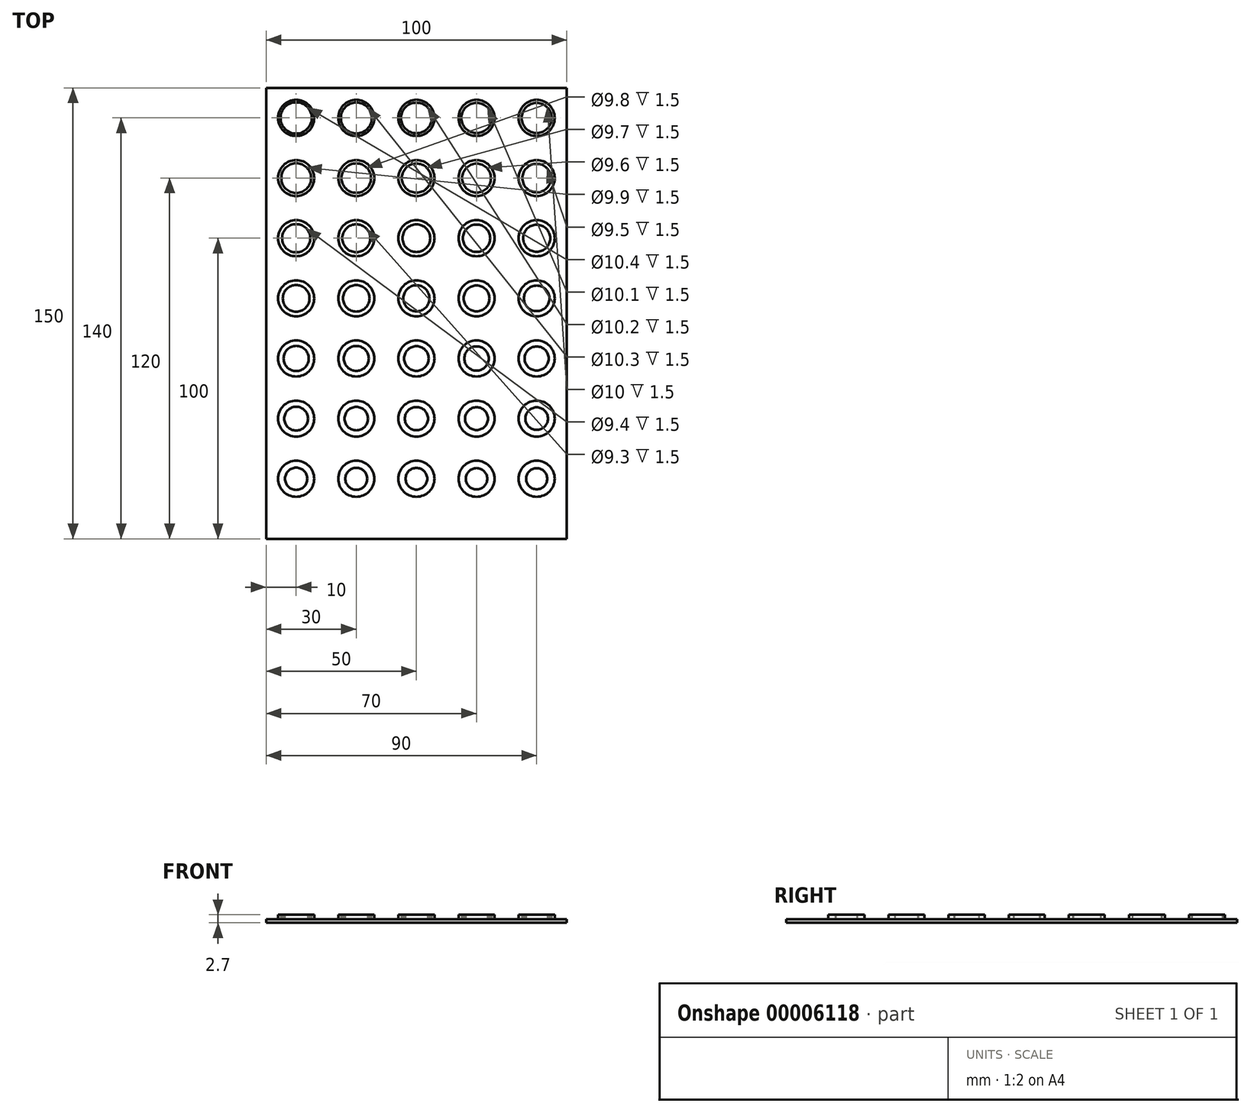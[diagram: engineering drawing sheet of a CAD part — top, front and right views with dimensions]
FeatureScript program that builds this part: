
annotation { "Feature Type Name" : "Feature", "Feature Type Description" : "" }
export const myFeature = defineFeature(function(context is Context, id is Id, definition is map)
    precondition{}
    {
        {
            var Q0;
            Q0=qCreatedBy(makeId("Top.planeOp"),FACE);
            var sketch = newSketch(context, id + "F0", { "sketchPlane" : qUnion([Q0])});
            skLineSegment(sketch, "E0.bottom", {"start": v(-10, 10) * mm, "end": v(90, 10) * mm});
            skLineSegment(sketch, "E0.top", {"start": v(-10, -140) * mm, "end": v(90, -140) * mm});
            skLineSegment(sketch, "E0.left", {"start": v(-10, 10) * mm, "end": v(-10, -140) * mm});
            skLineSegment(sketch, "E0.right", {"start": v(90, 10) * mm, "end": v(90, -140) * mm});
            skSolve(sketch);
        }
        {
            var Q0;
            Q0 = qSketchRegion(id + "F0", true);
            extrude(context, id + "F1", {"entities" : qUnion([Q0]), "depth" : 1.2 * mm});
        }
        {
            var Q0;
            Q0=makeQuery(id+"F1.opExtrude","CAP_FACE",FACE,{"disambiguationData":[OSD([sQuery(id+"F0.wireOp",EDGE,"E0.bottom"),sQuery(id+"F0.wireOp",EDGE,"E0.top"),sQuery(id+"F0.wireOp",EDGE,"E0.left"),sQuery(id+"F0.wireOp",EDGE,"E0.right")])],"isStart":false});
            var sketch = newSketch(context, id + "F2", { "sketchPlane" : qUnion([Q0])});
            skCircle(sketch, "E1", {"center": v(20, -20) * mm, "radius": 6 * mm});
            skCircle(sketch, "E2", {"center": v(20, -20) * mm, "radius": 4.9 * mm});
            skCircle(sketch, "E3", {"center": v(40, -20) * mm, "radius": 6 * mm});
            skCircle(sketch, "E4", {"center": v(40, -20) * mm, "radius": 4.85 * mm});
            skCircle(sketch, "E5", {"center": v(60, -20) * mm, "radius": 6 * mm});
            skCircle(sketch, "E6", {"center": v(60, -20) * mm, "radius": 4.8 * mm});
            skCircle(sketch, "E7", {"center": v(0, -20) * mm, "radius": 6 * mm});
            skCircle(sketch, "E8", {"center": v(0, -20) * mm, "radius": 4.95 * mm});
            skCircle(sketch, "E9", {"center": v(80, -20) * mm, "radius": 6 * mm});
            skCircle(sketch, "E10", {"center": v(80, -20) * mm, "radius": 4.75 * mm});
            skCircle(sketch, "E11", {"center": v(0, 0) * mm, "radius": 6 * mm});
            skCircle(sketch, "E12", {"center": v(60, 0) * mm, "radius": 6 * mm});
            skCircle(sketch, "E13", {"center": v(60, 0) * mm, "radius": 5.05 * mm});
            skCircle(sketch, "E14", {"center": v(0, 0) * mm, "radius": 5.2 * mm});
            skCircle(sketch, "E15", {"center": v(40, 0) * mm, "radius": 5.1 * mm});
            skCircle(sketch, "E16", {"center": v(40, 0) * mm, "radius": 6 * mm});
            skCircle(sketch, "E17", {"center": v(20, 0) * mm, "radius": 6 * mm});
            skCircle(sketch, "E18", {"center": v(20, 0) * mm, "radius": 5.15 * mm});
            skCircle(sketch, "E19", {"center": v(80, 0) * mm, "radius": 6 * mm});
            skCircle(sketch, "E20", {"center": v(80, 0) * mm, "radius": 5 * mm});
            skCircle(sketch, "E21", {"center": v(0, -60) * mm, "radius": 6 * mm});
            skCircle(sketch, "E22", {"center": v(80, -60) * mm, "radius": 6 * mm});
            skCircle(sketch, "E23", {"center": v(0, -60) * mm, "radius": 4.45 * mm});
            skCircle(sketch, "E24", {"center": v(60, -60) * mm, "radius": 4.3 * mm});
            skCircle(sketch, "E25", {"center": v(80, -60) * mm, "radius": 4.25 * mm});
            skCircle(sketch, "E26", {"center": v(60, -60) * mm, "radius": 6 * mm});
            skCircle(sketch, "E27", {"center": v(0, -40) * mm, "radius": 6 * mm});
            skCircle(sketch, "E28", {"center": v(40, -40) * mm, "radius": 6 * mm});
            skCircle(sketch, "E29", {"center": v(0, -40) * mm, "radius": 4.7 * mm});
            skCircle(sketch, "E30", {"center": v(40, -40) * mm, "radius": 4.6 * mm});
            skCircle(sketch, "E31", {"center": v(60, -40) * mm, "radius": 6 * mm});
            skCircle(sketch, "E32", {"center": v(60, -40) * mm, "radius": 4.55 * mm});
            skCircle(sketch, "E33", {"center": v(40, -60) * mm, "radius": 6 * mm});
            skCircle(sketch, "E34", {"center": v(20, -40) * mm, "radius": 6 * mm});
            skCircle(sketch, "E35", {"center": v(20, -40) * mm, "radius": 4.65 * mm});
            skCircle(sketch, "E36", {"center": v(20, -60) * mm, "radius": 6 * mm});
            skCircle(sketch, "E37", {"center": v(80, -40) * mm, "radius": 6 * mm});
            skCircle(sketch, "E38", {"center": v(80, -40) * mm, "radius": 4.5 * mm});
            skCircle(sketch, "E39", {"center": v(40, -60) * mm, "radius": 4.35 * mm});
            skCircle(sketch, "E40", {"center": v(20, -60) * mm, "radius": 4.4 * mm});
            skCircle(sketch, "E41", {"center": v(0, -80) * mm, "radius": 6 * mm});
            skCircle(sketch, "E42", {"center": v(0, -80) * mm, "radius": 4.2 * mm});
            skCircle(sketch, "E43", {"center": v(40, -80) * mm, "radius": 6 * mm});
            skCircle(sketch, "E44", {"center": v(40, -80) * mm, "radius": 4.1 * mm});
            skCircle(sketch, "E45", {"center": v(80, -80) * mm, "radius": 6 * mm});
            skCircle(sketch, "E46", {"center": v(80, -80) * mm, "radius": 4 * mm});
            skCircle(sketch, "E47", {"center": v(60, -80) * mm, "radius": 6 * mm});
            skCircle(sketch, "E48", {"center": v(20, -80) * mm, "radius": 6 * mm});
            skCircle(sketch, "E49", {"center": v(60, -80) * mm, "radius": 4.05 * mm});
            skCircle(sketch, "E50", {"center": v(20, -80) * mm, "radius": 4.15 * mm});
            skCircle(sketch, "E51", {"center": v(40, -120) * mm, "radius": 3.6 * mm});
            skCircle(sketch, "E52", {"center": v(80, -120) * mm, "radius": 3.5 * mm});
            skCircle(sketch, "E53", {"center": v(80, -120) * mm, "radius": 6 * mm});
            skCircle(sketch, "E54", {"center": v(60, -120) * mm, "radius": 6 * mm});
            skCircle(sketch, "E55", {"center": v(20, -120) * mm, "radius": 6 * mm});
            skCircle(sketch, "E56", {"center": v(60, -120) * mm, "radius": 3.55 * mm});
            skCircle(sketch, "E57", {"center": v(40, -100) * mm, "radius": 6 * mm});
            skCircle(sketch, "E58", {"center": v(20, -120) * mm, "radius": 3.65 * mm});
            skCircle(sketch, "E59", {"center": v(20, -100) * mm, "radius": 6 * mm});
            skCircle(sketch, "E60", {"center": v(0, -100) * mm, "radius": 6 * mm});
            skCircle(sketch, "E61", {"center": v(80, -100) * mm, "radius": 6 * mm});
            skCircle(sketch, "E62", {"center": v(40, -100) * mm, "radius": 3.85 * mm});
            skCircle(sketch, "E63", {"center": v(0, -100) * mm, "radius": 3.95 * mm});
            skCircle(sketch, "E64", {"center": v(20, -100) * mm, "radius": 3.9 * mm});
            skCircle(sketch, "E65", {"center": v(60, -100) * mm, "radius": 3.8 * mm});
            skCircle(sketch, "E66", {"center": v(0, -120) * mm, "radius": 6 * mm});
            skCircle(sketch, "E67", {"center": v(80, -100) * mm, "radius": 3.75 * mm});
            skCircle(sketch, "E68", {"center": v(0, -120) * mm, "radius": 3.7 * mm});
            skCircle(sketch, "E69", {"center": v(60, -100) * mm, "radius": 6 * mm});
            skCircle(sketch, "E70", {"center": v(40, -120) * mm, "radius": 6 * mm});
            skSolve(sketch);
        }
        {
            var Q0;
            Q0 = qSketchRegion(id + "F2", true);
            extrude(context, id + "F3", {"entities" : qUnion([Q0]), "operationType" : NewBodyOperationType.ADD, "depth" : 1.5 * mm});
        }
    });
